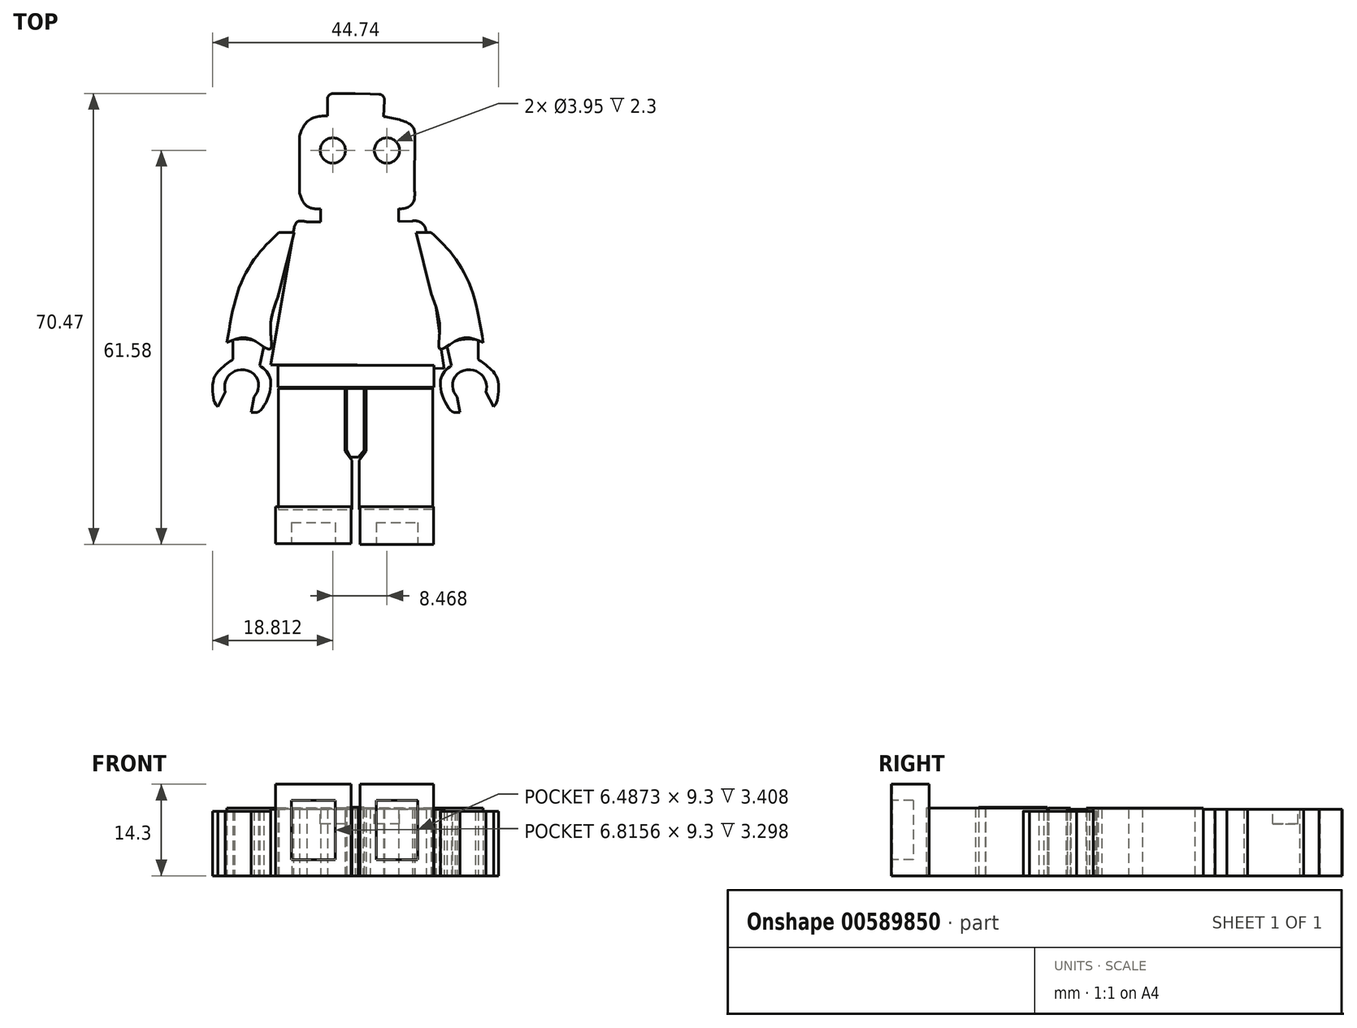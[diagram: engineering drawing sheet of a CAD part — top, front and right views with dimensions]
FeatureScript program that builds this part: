
annotation { "Feature Type Name" : "Feature", "Feature Type Description" : "" }
export const myFeature = defineFeature(function(context is Context, id is Id, definition is map)
    precondition{}
    {
        {
            var Q0;
            Q0=qCreatedBy(makeId("Top.planeOp"),FACE);
            var sketch = newSketch(context, id + "F0", { "sketchPlane" : qUnion([Q0])});
            skLineSegment(sketch, "E0", {"start": v(-32.03, 58.05) * mm, "end": v(-32.03, 66.76) * mm});
            skFitSpline(sketch, "E1", {"points": [v(-32.03, 66.76) * mm, v(-30.41, 69.34) * mm, v(-27.64, 69.93) * mm], "startDerivative": vector(2.04, 6.1) * mm, "endDerivative": vector(6.3, 0.23) * mm});
            skLineSegment(sketch, "E2", {"start": v(-27.64, 69.93) * mm, "end": v(-27.64, 72.54) * mm});
            skLineSegment(sketch, "E3", {"start": v(-26.77, 73.4) * mm, "end": v(-23.32, 73.4) * mm});
            skFitSpline(sketch, "E4", {"points": [v(-32.03, 58.05) * mm, v(-30.85, 55.83) * mm, v(-28.73, 55.35) * mm], "startDerivative": vector(1.2, -5.2) * mm, "endDerivative": vector(4.97, -0.15) * mm});
            skLineSegment(sketch, "E5", {"start": v(-28.73, 55.35) * mm, "end": v(-28.73, 53.35) * mm});
            skLineSegment(sketch, "E6", {"start": v(-28.73, 53.35) * mm, "end": v(-30.85, 53.35) * mm});
            skFitSpline(sketch, "E7", {"points": [v(-30.85, 53.35) * mm, v(-32.39, 53.35) * mm, v(-32.98, 51.59) * mm], "startDerivative": vector(-3.72, 0.8) * mm, "endDerivative": vector(-0.57, -4.25) * mm});
            skLineSegment(sketch, "E8", {"start": v(-32.98, 51.59) * mm, "end": v(-36.5, 30.97) * mm});
            skLineSegment(sketch, "E9", {"start": v(-36.5, 30.97) * mm, "end": v(-22.96, 30.97) * mm});
            skLineSegment(sketch, "E10.MirrorCS", {"start": v(-18.83, 69.8) * mm, "end": v(-18.73, 72.4) * mm});
            skLineSegment(sketch, "E11.MirrorCS", {"start": v(-16.52, 53.42) * mm, "end": v(-14.37, 53.5) * mm});
            skLineSegment(sketch, "E12.MirrorCS", {"start": v(-16.52, 55.42) * mm, "end": v(-16.52, 53.42) * mm});
            skFitSpline(sketch, "E13.MirrorCS", {"points": [v(-14.37, 53.5) * mm, v(-12.67, 52.96) * mm, v(-12.15, 51.18) * mm], "startDerivative": vector(3.75, 0.65) * mm, "endDerivative": vector(0.4, -4.27) * mm});
            skFitSpline(sketch, "E14.MirrorCS", {"points": [v(-13.94, 67.35) * mm, v(-14.92, 68.75) * mm, v(-18.83, 69.8) * mm], "startDerivative": vector(-1.8, 6.17) * mm, "endDerivative": vector(-6.28, 0.47) * mm});
            skLineSegment(sketch, "E15.MirrorCS", {"start": v(-12.15, 51.18) * mm, "end": v(-9.43, 30.44) * mm});
            skLineSegment(sketch, "E16.MirrorCS", {"start": v(-14.02, 58.63) * mm, "end": v(-13.94, 67.35) * mm});
            skLineSegment(sketch, "E17.MirrorCS", {"start": v(-19.56, 73.3) * mm, "end": v(-20.94, 73.36) * mm});
            skLineSegment(sketch, "E18.MirrorCS", {"start": v(-9.43, 30.44) * mm, "end": v(-22.96, 30.97) * mm});
            skLineSegment(sketch, "E19", {"start": v(-23.32, 73.4) * mm, "end": v(-20.94, 73.36) * mm});
            skPoint(sketch, "E20.visualSharp", {"position": v(-18.7, 73.27) * mm});
            skArc(sketch, "E20.filletArc", {"start": v(-18.73, 72.4) * mm, "mid": v(-18.96, 73.03) * mm, "end": v(-19.56, 73.3) * mm});
            skPoint(sketch, "E21.visualSharp", {"position": v(-27.64, 73.4) * mm});
            skArc(sketch, "E21.filletArc", {"start": v(-26.77, 73.4) * mm, "mid": v(-27.38, 73.15) * mm, "end": v(-27.64, 72.54) * mm});
            skFitSpline(sketch, "E22", {"points": [v(-32.4, 58.09) * mm, v(-31.23, 55.87) * mm, v(-29.1, 55.4) * mm], "startDerivative": vector(1.2, -5.2) * mm, "endDerivative": vector(4.97, -0.15) * mm});
            skFitSpline(sketch, "E23", {"points": [v(-16.52, 55.42) * mm, v(-14.34, 56.23) * mm, v(-14.02, 58.63) * mm], "startDerivative": vector(4.64, -0.69) * mm, "endDerivative": vector(-0.04, 4.97) * mm});
            skPoint(sketch, "E24", {"position": v(-16.52, 54.42) * mm});
            skSolve(sketch);
        }
        {
            var Q0;
            Q0=qCreatedBy(makeId("Top.planeOp"),FACE);
            var sketch = newSketch(context, id + "F1", { "sketchPlane" : qUnion([Q0])});
            skLineSegment(sketch, "E25", {"start": v(-32.86, 51.7) * mm, "end": v(-35.21, 51.7) * mm});
            skFitSpline(sketch, "E26", {"points": [v(-35.21, 51.7) * mm, v(-38.4, 48.4) * mm, v(-41.46, 42.99) * mm, v(-43.34, 34.5) * mm], "startDerivative": vector(-11.5, -10.8) * mm, "endDerivative": vector(-3.71, -23) * mm});
            skFitSpline(sketch, "E27", {"points": [v(-35.21, 42.16) * mm, v(-36.27, 38.86) * mm, v(-36.5, 35.92) * mm, v(-36.63, 33.44) * mm, v(-39.69, 35.1) * mm, v(-43.34, 34.5) * mm], "startDerivative": vector(-5.87, -16.36) * mm, "endDerivative": vector(-16.51, -7.35) * mm});
            skLineSegment(sketch, "E28", {"start": v(-35.21, 42.16) * mm, "end": v(-32.86, 51.7) * mm});
            skLineSegment(sketch, "E29.MirrorCS", {"start": v(-13.77, 51.7) * mm, "end": v(-11.42, 51.7) * mm});
            skFitSpline(sketch, "E30.MirrorCS", {"points": [v(-11.42, 51.7) * mm, v(-8.24, 48.4) * mm, v(-5.17, 42.99) * mm, v(-3.29, 34.5) * mm], "startDerivative": vector(11.5, -10.8) * mm, "endDerivative": vector(3.71, -23) * mm});
            skFitSpline(sketch, "E31.MirrorCS", {"points": [v(-11.42, 42.16) * mm, v(-10.36, 38.86) * mm, v(-10.12, 35.92) * mm, v(-10, 33.44) * mm, v(-6.94, 35.1) * mm, v(-3.29, 34.5) * mm], "startDerivative": vector(5.87, -16.36) * mm, "endDerivative": vector(16.51, -7.35) * mm});
            skLineSegment(sketch, "E32.MirrorCS", {"start": v(-11.42, 42.16) * mm, "end": v(-13.77, 51.7) * mm});
            skSolve(sketch);
        }
        {
            var Q0;
            Q0=qCreatedBy(makeId("Top.planeOp"),FACE);
            var sketch = newSketch(context, id + "F2", { "sketchPlane" : qUnion([Q0])});
            skLineSegment(sketch, "E33", {"start": v(-42.4, 34.97) * mm, "end": v(-42.4, 31.9) * mm});
            skLineSegment(sketch, "E34", {"start": v(-37.48, 34.22) * mm, "end": v(-38.23, 30.9) * mm});
            skFitSpline(sketch, "E35", {"points": [v(-38.23, 30.9) * mm, v(-36.9, 29.64) * mm, v(-36.57, 27.14) * mm, v(-38.23, 23.81) * mm, v(-39.57, 23.56) * mm], "startDerivative": vector(6.74, -4.84) * mm, "endDerivative": vector(-6.94, 0.58) * mm});
            skFitSpline(sketch, "E36", {"points": [v(-42.4, 31.9) * mm, v(-43.73, 30.9) * mm, v(-45.4, 28.8) * mm, v(-45.23, 25.06) * mm, v(-44.57, 24.31) * mm], "startDerivative": vector(-5.75, -4.21) * mm, "endDerivative": vector(4.19, -2.91) * mm});
            skLineSegment(sketch, "E37", {"start": v(-44.8, 24.48) * mm, "end": v(-43.65, 26.73) * mm});
            skLineSegment(sketch, "E38", {"start": v(-39.57, 23.56) * mm, "end": v(-39.12, 25.98) * mm});
            skFitSpline(sketch, "E39", {"points": [v(-43.65, 26.73) * mm, v(-43.65, 28.23) * mm, v(-42.82, 29.56) * mm, v(-41.32, 30.23) * mm, v(-39.15, 29.56) * mm, v(-38.4, 27.56) * mm, v(-39.12, 25.98) * mm], "startDerivative": vector(-1.18, 9.98) * mm, "endDerivative": vector(-6.03, -8.94) * mm});
            skFitSpline(sketch, "E40", {"points": [v(-42.4, 34.97) * mm, v(-39.78, 34.97) * mm, v(-37.48, 34.22) * mm], "startDerivative": vector(5.24, 0.39) * mm, "endDerivative": vector(4.58, -1.9) * mm});
            skLineSegment(sketch, "E41.MirrorCS", {"start": v(-6.92, 23.56) * mm, "end": v(-7.36, 25.98) * mm});
            skLineSegment(sketch, "E42.MirrorCS", {"start": v(-1.68, 24.48) * mm, "end": v(-2.83, 26.73) * mm});
            skLineSegment(sketch, "E43.MirrorCS", {"start": v(-4.08, 34.97) * mm, "end": v(-4.08, 31.9) * mm});
            skFitSpline(sketch, "E44.MirrorCS", {"points": [v(-8.25, 30.9) * mm, v(-9.58, 29.64) * mm, v(-9.91, 27.14) * mm, v(-8.25, 23.81) * mm, v(-6.92, 23.56) * mm], "startDerivative": vector(-6.74, -4.84) * mm, "endDerivative": vector(6.94, 0.58) * mm});
            skLineSegment(sketch, "E45.MirrorCS", {"start": v(-9, 34.22) * mm, "end": v(-8.25, 30.9) * mm});
            skFitSpline(sketch, "E46.MirrorCS", {"points": [v(-2.83, 26.73) * mm, v(-2.83, 28.23) * mm, v(-3.66, 29.56) * mm, v(-5.17, 30.23) * mm, v(-7.33, 29.56) * mm, v(-8.08, 27.56) * mm, v(-7.36, 25.98) * mm], "startDerivative": vector(1.18, 9.98) * mm, "endDerivative": vector(6.03, -8.94) * mm});
            skFitSpline(sketch, "E47.MirrorCS", {"points": [v(-4.08, 34.97) * mm, v(-6.7, 34.97) * mm, v(-9, 34.22) * mm], "startDerivative": vector(-5.24, 0.39) * mm, "endDerivative": vector(-4.58, -1.9) * mm});
            skFitSpline(sketch, "E48.MirrorCS", {"points": [v(-4.08, 31.9) * mm, v(-2.75, 30.9) * mm, v(-1.08, 28.8) * mm, v(-1.25, 25.06) * mm, v(-1.92, 24.31) * mm], "startDerivative": vector(5.75, -4.21) * mm, "endDerivative": vector(-4.19, -2.91) * mm});
            skSolve(sketch);
        }
        {
            var Q0;
            Q0=qCreatedBy(makeId("Top.planeOp"),FACE);
            var sketch = newSketch(context, id + "F3", { "sketchPlane" : qUnion([Q0])});
            skLineSegment(sketch, "E49", {"start": v(-35.3, 8.4) * mm, "end": v(-23.8, 8.4) * mm});
            skLineSegment(sketch, "E50", {"start": v(-23.8, 8.4) * mm, "end": v(-23.8, 16.06) * mm});
            skLineSegment(sketch, "E51", {"start": v(-23.8, 16.06) * mm, "end": v(-24.9, 17.56) * mm});
            skLineSegment(sketch, "E52", {"start": v(-24.9, 17.56) * mm, "end": v(-24.9, 27.3) * mm});
            skLineSegment(sketch, "E53", {"start": v(-24.9, 27.3) * mm, "end": v(-35.3, 27.3) * mm});
            skLineSegment(sketch, "E54", {"start": v(-35.3, 27.3) * mm, "end": v(-35.3, 8.4) * mm});
            skLineSegment(sketch, "E55.MirrorCS", {"start": v(-22.64, 16.06) * mm, "end": v(-21.56, 17.56) * mm});
            skLineSegment(sketch, "E56.MirrorCS", {"start": v(-21.56, 27.3) * mm, "end": v(-11.15, 27.3) * mm});
            skLineSegment(sketch, "E57.MirrorCS", {"start": v(-11.15, 27.3) * mm, "end": v(-11.15, 8.4) * mm});
            skLineSegment(sketch, "E58.MirrorCS", {"start": v(-11.15, 8.4) * mm, "end": v(-22.64, 8.4) * mm});
            skLineSegment(sketch, "E59.MirrorCS", {"start": v(-21.56, 17.56) * mm, "end": v(-21.56, 27.3) * mm});
            skLineSegment(sketch, "E60.MirrorCS", {"start": v(-22.64, 8.4) * mm, "end": v(-22.64, 16.06) * mm});
            skSolve(sketch);
        }
        {
            var Q0;
            Q0=qCreatedBy(makeId("Top.planeOp"),FACE);
            var sketch = newSketch(context, id + "F4", { "sketchPlane" : qUnion([Q0])});
            skLineSegment(sketch, "E61", {"start": v(-24.64, 27.3) * mm, "end": v(-24.64, 17.65) * mm});
            skLineSegment(sketch, "E62", {"start": v(-24.64, 17.65) * mm, "end": v(-24.06, 16.56) * mm});
            skLineSegment(sketch, "E63", {"start": v(-24.06, 16.56) * mm, "end": v(-22.8, 16.56) * mm});
            skLineSegment(sketch, "E64", {"start": v(-22.8, 16.56) * mm, "end": v(-21.9, 17.65) * mm});
            skLineSegment(sketch, "E65", {"start": v(-21.9, 17.65) * mm, "end": v(-21.9, 27.3) * mm});
            skLineSegment(sketch, "E66", {"start": v(-21.9, 27.3) * mm, "end": v(-24.64, 27.3) * mm});
            skSolve(sketch);
        }
        {
            var Q0;
            Q0=qCreatedBy(makeId("Top.planeOp"),FACE);
            var sketch = newSketch(context, id + "F5", { "sketchPlane" : qUnion([Q0])});
            skLineSegment(sketch, "E67.bottom", {"start": v(-35.75, 8.85) * mm, "end": v(-23.94, 8.85) * mm});
            skLineSegment(sketch, "E67.top", {"start": v(-35.75, 3.05) * mm, "end": v(-23.94, 3.05) * mm});
            skLineSegment(sketch, "E67.left", {"start": v(-35.75, 8.85) * mm, "end": v(-35.75, 3.05) * mm});
            skLineSegment(sketch, "E67.right", {"start": v(-23.94, 8.85) * mm, "end": v(-23.94, 3.05) * mm});
            skLineSegment(sketch, "E68.bottom", {"start": v(-22.52, 8.85) * mm, "end": v(-11.03, 8.85) * mm});
            skLineSegment(sketch, "E68.top", {"start": v(-22.52, 2.94) * mm, "end": v(-11.03, 2.94) * mm});
            skLineSegment(sketch, "E68.left", {"start": v(-22.52, 8.85) * mm, "end": v(-22.52, 2.94) * mm});
            skLineSegment(sketch, "E68.right", {"start": v(-11.03, 8.85) * mm, "end": v(-11.03, 2.94) * mm});
            skSolve(sketch);
        }
        {
            var Q0;
            Q0 = qSketchRegion(id + "F0", true);
            extrude(context, id + "F6", {"entities" : qUnion([Q0]), "depth" : 10.4 * mm, "offsetDistance" : 25 * mm});
        }
        {
            var Q0;
            Q0 = qSketchRegion(id + "F1", true);
            extrude(context, id + "F7", {"entities" : qUnion([Q0]), "operationType" : NewBodyOperationType.ADD, "depth" : 10.6 * mm, "offsetDistance" : 25 * mm});
        }
        {
            var Q0;
            Q0 = qSketchRegion(id + "F3", true);
            extrude(context, id + "F8", {"entities" : qUnion([Q0]), "depth" : 10.6 * mm, "offsetDistance" : 25 * mm});
        }
        {
            var Q0;
            Q0 = qSketchRegion(id + "F4", true);
            extrude(context, id + "F9", {"entities" : qUnion([Q0]), "depth" : 10.7 * mm, "offsetDistance" : 25 * mm});
        }
        {
            var Q0;
            Q0 = qSketchRegion(id + "F5", true);
            extrude(context, id + "F10", {"entities" : qUnion([Q0]), "depth" : 14.3 * mm, "offsetDistance" : 25 * mm});
        }
        {
            var Q0;
            Q0=qCreatedBy(makeId("Top.planeOp"),FACE);
            var sketch = newSketch(context, id + "F11", { "sketchPlane" : qUnion([Q0])});
            skLineSegment(sketch, "E69.bottom", {"start": v(-35.37, 30.94) * mm, "end": v(-10.97, 30.94) * mm});
            skLineSegment(sketch, "E69.top", {"start": v(-35.37, 27.5) * mm, "end": v(-10.97, 27.5) * mm});
            skLineSegment(sketch, "E69.left", {"start": v(-35.37, 30.94) * mm, "end": v(-35.37, 27.5) * mm});
            skLineSegment(sketch, "E69.right", {"start": v(-10.97, 30.94) * mm, "end": v(-10.97, 27.5) * mm});
            skSolve(sketch);
        }
        {
            var Q0;
            Q0 = qSketchRegion(id + "F2", true);
            extrude(context, id + "F12", {"entities" : qUnion([Q0]), "operationType" : NewBodyOperationType.ADD, "depth" : 10.1 * mm, "offsetDistance" : 25 * mm});
        }
        {
            var Q0;
            Q0 = qSketchRegion(id + "F11", true);
            extrude(context, id + "F13", {"entities" : qUnion([Q0]), "operationType" : NewBodyOperationType.ADD, "depth" : 10.6 * mm, "offsetDistance" : 25 * mm});
        }
        {
            var Q0;
            Q0=makeQuery(id+"F10.opExtrude","SWEPT_FACE",FACE,{"disambiguationData":[OSD([sQuery(id+"F5.wireOp",EDGE,"E67.top")])]});
            shell(context, id + "F14", {"entities" : qUnion([Q0]), "thickness" : 2.5 * mm});
        }
        {
            var Q0;
            Q0=makeQuery(id+"F10.opExtrude","SWEPT_FACE",FACE,{"disambiguationData":[OSD([sQuery(id+"F5.wireOp",EDGE,"E68.top")])]});
            shell(context, id + "F15", {"entities" : qUnion([Q0]), "thickness" : 2.5 * mm});
        }
        {
            var Q0;
            Q0=makeQuery(id+"F6.opExtrude","CAP_FACE",FACE,{"disambiguationData":[OSD([sQuery(id+"F0.wireOp",EDGE,"E0"),sQuery(id+"F0.wireOp",EDGE,"E1"),sQuery(id+"F0.wireOp",EDGE,"E2"),sQuery(id+"F0.wireOp",EDGE,"E3"),sQuery(id+"F0.wireOp",EDGE,"E4"),sQuery(id+"F0.wireOp",EDGE,"E5"),sQuery(id+"F0.wireOp",EDGE,"E6"),sQuery(id+"F0.wireOp",EDGE,"E7"),sQuery(id+"F0.wireOp",EDGE,"E8"),sQuery(id+"F0.wireOp",EDGE,"E9"),sQuery(id+"F0.wireOp",EDGE,"E10.MirrorCS"),sQuery(id+"F0.wireOp",EDGE,"E11.MirrorCS"),sQuery(id+"F0.wireOp",EDGE,"E12.MirrorCS"),sQuery(id+"F0.wireOp",EDGE,"E13.MirrorCS"),sQuery(id+"F0.wireOp",EDGE,"E14.MirrorCS"),sQuery(id+"F0.wireOp",EDGE,"E15.MirrorCS"),sQuery(id+"F0.wireOp",EDGE,"E16.MirrorCS"),sQuery(id+"F0.wireOp",EDGE,"E17.MirrorCS"),sQuery(id+"F0.wireOp",EDGE,"E18.MirrorCS"),sQuery(id+"F0.wireOp",EDGE,"E19"),sQuery(id+"F0.wireOp",EDGE,"E20.filletArc"),sQuery(id+"F0.wireOp",EDGE,"E21.filletArc"),sQuery(id+"F0.wireOp",EDGE,"E23")])],"isStart":false});
            var sketch = newSketch(context, id + "F16", { "sketchPlane" : qUnion([Q0])});
            skCircle(sketch, "E70", {"center": v(-26.8, 64.52) * mm, "radius": 1.98 * mm});
            skCircle(sketch, "E71.MirrorC", {"center": v(-18.33, 64.52) * mm, "radius": 1.98 * mm});
            skSolve(sketch);
        }
        {
            var Q0;
            Q0 = qSketchRegion(id + "F16", true);
            extrude(context, id + "F17", {"entities" : qUnion([Q0]), "operationType" : NewBodyOperationType.REMOVE, "oppositeDirection" : true, "depth" : 2.3 * mm, "offsetDistance" : 25 * mm});
        }
    });
